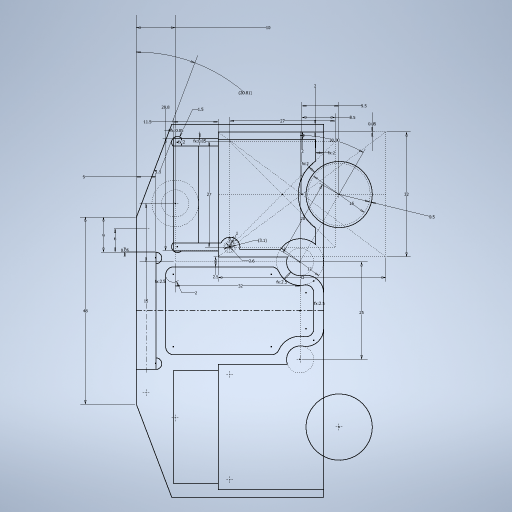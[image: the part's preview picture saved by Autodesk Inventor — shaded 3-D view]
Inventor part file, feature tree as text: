
AUTODESK INVENTOR PART (.ipt)
format: ipt  version: 2024.2 (Build 282272000, 272)  size: 328,192 bytes
history: native  units: mm
features: sketch x1
ambient origin geometry x8: Origin, YZ Plane, XZ Plane, XY Plane, X Axis, Y Axis, Z Axis, Center Point
feature tree (1):
  sketch  "Sketch1"  dims[d1=25.0mm d2=32.0mm d3=15.0mm d4=20.0mm d5=30.0deg d6=43.0mm d7=32.0mm d8=27.0mm d9=27.0mm d10=9.5mm d11=8.5mm d12=16.0mm d13=12.0mm d14=28.8mm d15=11.5mm d16=0.5mm d17=2.0mm d18=0.05mm d22=3.632168mm d23=0.05mm d24=0.05mm d39=2.0mm d40=2.0mm d41=2.0mm d42=2.0mm d46=2.0mm d52=1.5mm d53=1.5mm d54=10.0mm d55=5.0mm d58=9.0mm d59=0.05mm d60=6.0mm d61=48.0mm d63=2.5mm d64=2.5mm d65=2.0mm d67=2.5mm d68=3.1mm d69=2.6mm d70=0.25mm d71=1.0mm d72=2.5mm]
